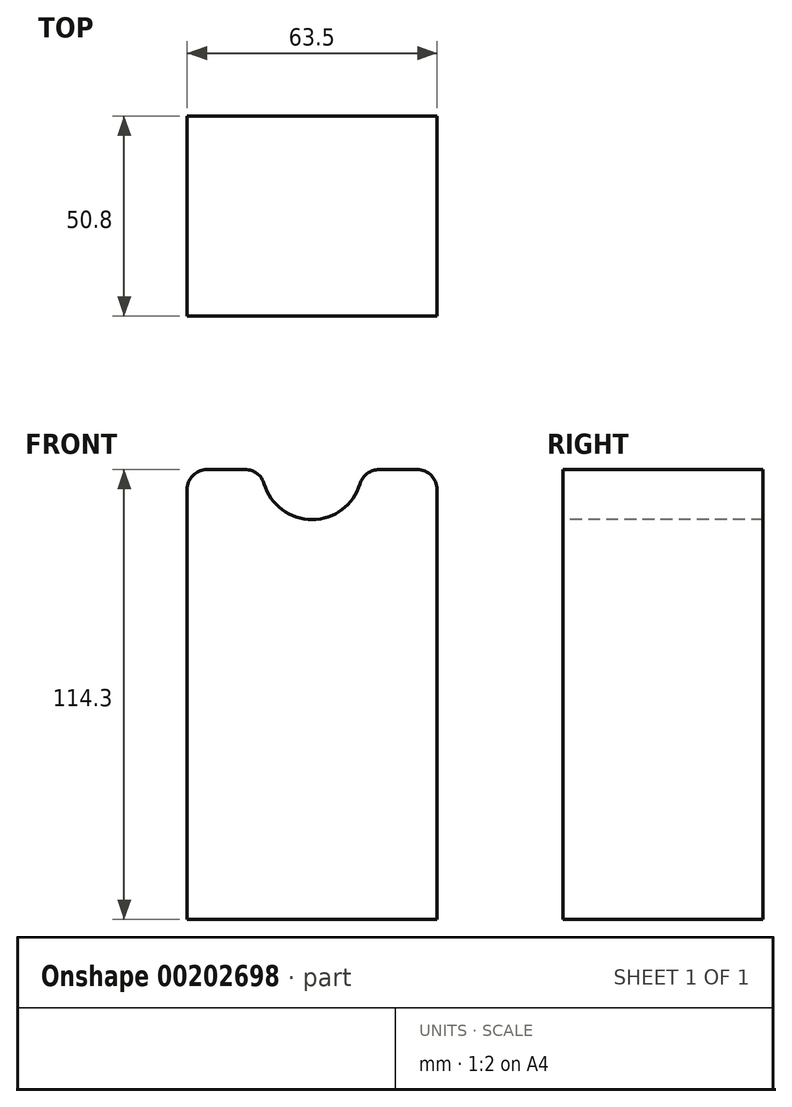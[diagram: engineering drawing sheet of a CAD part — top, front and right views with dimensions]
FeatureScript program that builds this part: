
annotation { "Feature Type Name" : "Feature", "Feature Type Description" : "" }
export const myFeature = defineFeature(function(context is Context, id is Id, definition is map)
    precondition{}
    {
        {
            var Q0;
            Q0=qCreatedBy(makeId("Front.planeOp"),FACE);
            var sketch = newSketch(context, id + "F0", { "sketchPlane" : qUnion([Q0])});
            skLineSegment(sketch, "E0.bottom", {"start": v(0, 0) * mm, "end": v(63.5, 0) * mm});
            skLineSegment(sketch, "E0.top", {"start": v(0, 114.3) * mm, "end": v(19.05, 114.3) * mm});
            skLineSegment(sketch, "E0.left", {"start": v(0, 0) * mm, "end": v(0, 114.3) * mm});
            skLineSegment(sketch, "E0.right", {"start": v(63.5, 0) * mm, "end": v(63.5, 114.3) * mm});
            skArc(sketch, "E1", {"start": v(19.05, 114.3) * mm, "mid": v(31.75, 101.6) * mm, "end": v(44.45, 114.3) * mm});
            skLineSegment(sketch, "E2.trimOffspring", {"start": v(44.45, 114.3) * mm, "end": v(63.5, 114.3) * mm});
            skSolve(sketch);
        }
        {
            var Q0;
            Q0=makeQuery(id+"F0.imprint","IMPRINT",FACE,{"disambiguationData":[TD([[makeQuery(id+"F0.imprint","IMPRINT",EDGE,{"derivedFrom":sQuery(id+"F0.wireOp",EDGE,"E0.bottom")}),1.0]])]});
            extrude(context, id + "F1", {"entities" : qUnion([Q0]), "oppositeDirection" : true, "depth" : 50.8 * mm});
        }
        {
            var Q0;
            Q0=makeQuery(id+"F1.opExtrude","SWEPT_EDGE",EDGE,{"disambiguationData":[OSD([sQuery(id+"F0.wireOp",EDGE,"E0.top"),sQuery(id+"F0.wireOp",EDGE,"E1")])]});
            fillet(context, id + "F2", {"entities" : qUnion([Q0]), "radius" : 5.08 * mm, "tangentPropagation" : true, "allowEdgeOverflow" : false});
        }
        {
            var Q0;
            Q0=makeQuery(id+"F1.opExtrude","SWEPT_EDGE",EDGE,{"disambiguationData":[OSD([sQuery(id+"F0.wireOp",EDGE,"E1"),sQuery(id+"F0.wireOp",EDGE,"E2.trimOffspring")])]});
            fillet(context, id + "F3", {"entities" : qUnion([Q0]), "radius" : 5.08 * mm, "tangentPropagation" : true, "allowEdgeOverflow" : false});
        }
        {
            var Q0;
            Q0=makeQuery(id+"F1.opExtrude","SWEPT_EDGE",EDGE,{"disambiguationData":[OSD([sQuery(id+"F0.wireOp",EDGE,"E0.right"),sQuery(id+"F0.wireOp",EDGE,"E2.trimOffspring")])]});
            fillet(context, id + "F4", {"entities" : qUnion([Q0]), "radius" : 5.08 * mm, "tangentPropagation" : true, "allowEdgeOverflow" : false});
        }
        {
            var Q0;
            Q0=makeQuery(id+"F1.opExtrude","SWEPT_EDGE",EDGE,{"disambiguationData":[OSD([sQuery(id+"F0.wireOp",EDGE,"E0.top"),sQuery(id+"F0.wireOp",EDGE,"E0.left")])]});
            fillet(context, id + "F5", {"entities" : qUnion([Q0]), "radius" : 5.08 * mm, "tangentPropagation" : true, "allowEdgeOverflow" : false});
        }
    });
